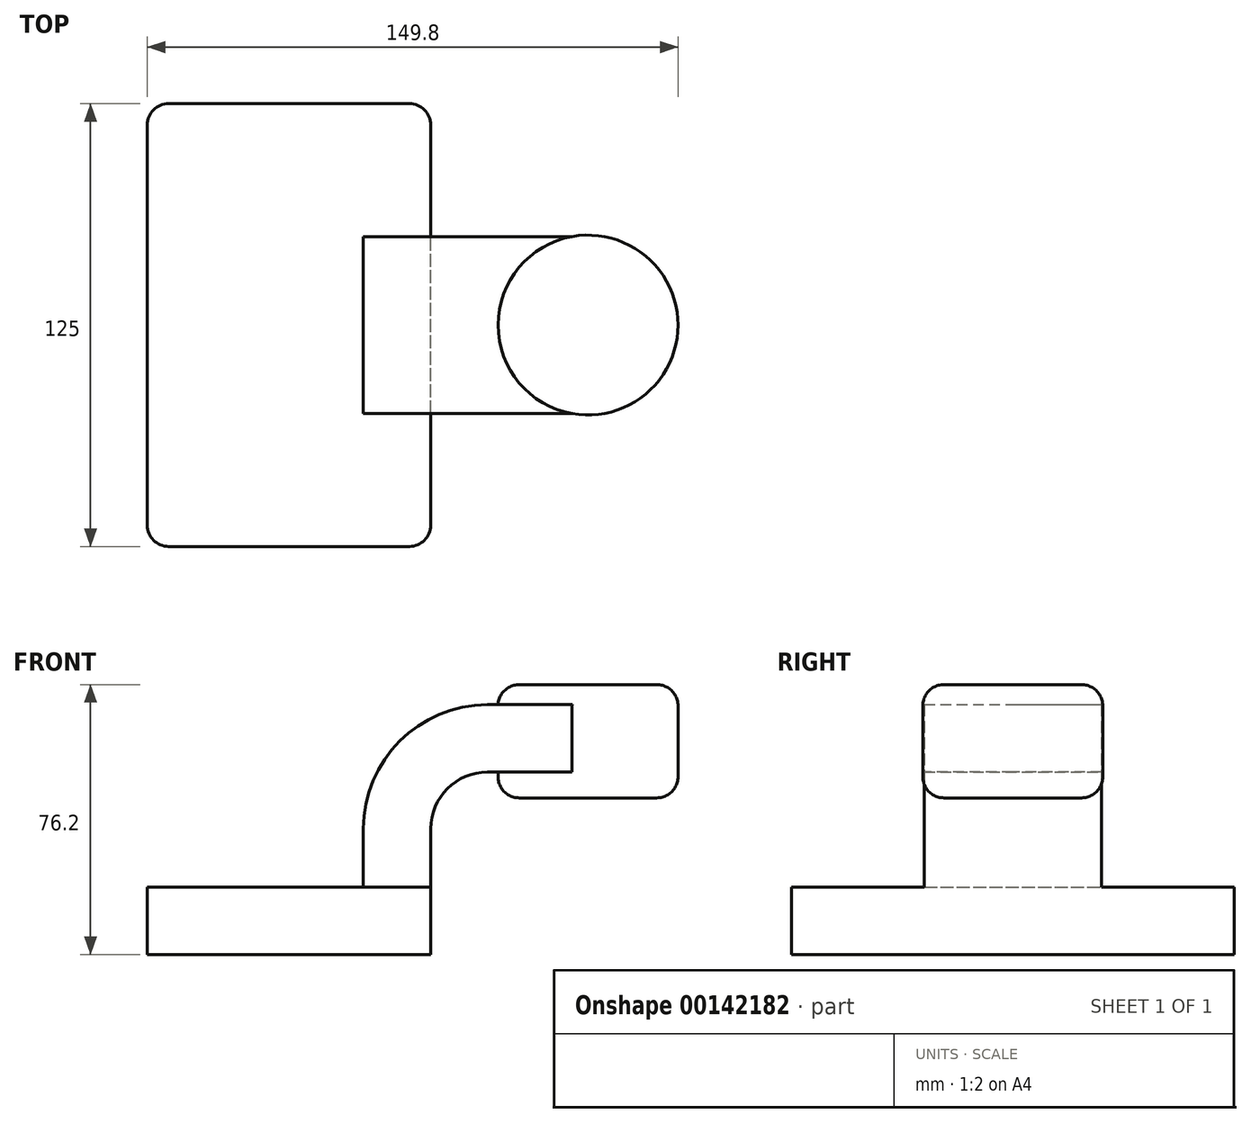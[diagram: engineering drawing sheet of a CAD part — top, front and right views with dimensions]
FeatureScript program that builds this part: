
annotation { "Feature Type Name" : "Feature", "Feature Type Description" : "" }
export const myFeature = defineFeature(function(context is Context, id is Id, definition is map)
    precondition{}
    {
        {
            var Q0;
            Q0=qCreatedBy(makeId("Front.planeOp"),FACE);
            var sketch = newSketch(context, id + "F0", { "sketchPlane" : qUnion([Q0])});
            skLineSegment(sketch, "E0.bottom", {"start": v(-40, -9.5) * mm, "end": v(40, -9.5) * mm});
            skLineSegment(sketch, "E0.top", {"start": v(-40, 9.5) * mm, "end": v(40, 9.5) * mm});
            skLineSegment(sketch, "E0.left", {"start": v(-40, -9.5) * mm, "end": v(-40, 9.5) * mm});
            skLineSegment(sketch, "E0.right", {"start": v(40, -9.5) * mm, "end": v(40, 9.5) * mm});
            skPoint(sketch, "E0.middle", {"position": v(0, 0) * mm});
            skLineSegment(sketch, "E1", {"start": v(40, 9.5) * mm, "end": v(40, 26) * mm});
            skArc(sketch, "E2", {"start": v(40, 26) * mm, "mid": v(44.69, 37.31) * mm, "end": v(56, 42) * mm});
            skLineSegment(sketch, "E3.bottom", {"start": v(59, 34.7) * mm, "end": v(109.8, 34.7) * mm});
            skLineSegment(sketch, "E3.top", {"start": v(59, 66.7) * mm, "end": v(109.8, 66.7) * mm});
            skLineSegment(sketch, "E3.left", {"start": v(59, 34.7) * mm, "end": v(59, 66.7) * mm});
            skLineSegment(sketch, "E3.right", {"start": v(109.8, 34.7) * mm, "end": v(109.8, 66.7) * mm});
            skPoint(sketch, "E3.middle", {"position": v(84.4, 50.7) * mm});
            skLineSegment(sketch, "E4", {"start": v(56, 42) * mm, "end": v(84.4, 42) * mm});
            skLineSegment(sketch, "E5.0", {"start": v(56, 61) * mm, "end": v(84.4, 61) * mm});
            skArc(sketch, "E5.1", {"start": v(21, 26) * mm, "mid": v(31.25, 50.75) * mm, "end": v(56, 61) * mm});
            skLineSegment(sketch, "E5.2", {"start": v(21, 9.5) * mm, "end": v(21, 26) * mm});
            skFitSpline(sketch, "E6", {"points": [v(-40, 9.5) * mm, v(56, 61) * mm], "startDerivative": vector(11.83, 64.45) * mm, "endDerivative": vector(168, -2.6) * mm});
            skLineSegment(sketch, "E7", {"start": v(84.4, 34.7) * mm, "end": v(84.4, 66.7) * mm});
            skSolve(sketch);
        }
        {
            var Q0;
            Q0=makeQuery(id+"F0.imprint","IMPRINT",FACE,{"disambiguationData":[TD([[makeQuery(id+"F0.imprint","IMPRINT",EDGE,{"derivedFrom":sQuery(id+"F0.wireOp",EDGE,"E0.bottom")}),1.0]])]});
            extrude(context, id + "F1", {"entities" : qUnion([Q0]), "endBound" : BoundingType.SYMMETRIC, "depth" : 125 * mm});
        }
        {
            var Q0;
            {var subQ5=sQuery(id+"F0.wireOp",EDGE,"E1");Q0=makeQuery(id+"F0.imprint","IMPRINT",FACE,{"disambiguationData":[TD([[makeQuery(id+"F0.imprint","IMPRINT",EDGE,{"derivedFrom":subQ5}),1.0]])]});}
            var Q1;
            {var subQ0=sQuery(id+"F0.wireOp",EDGE,"E4");var subQ1=sQuery(id+"F0.wireOp",EDGE,"E3.left");var subQ2=makeQuery(id+"F0.imprint","INTERSECT",VERTEX,{"derivedFrom":[subQ1,subQ0]});Q1=makeQuery(id+"F0.imprint","IMPRINT",FACE,{"disambiguationData":[TD([[makeQuery(id+"F0.imprint","IMPRINT",EDGE,{"disambiguationData":[TD([[subQ2,-1.0]])],"derivedFrom":subQ1}),-1.0]])]});}
            extrude(context, id + "F2", {"entities" : qUnion([Q0, Q1]), "operationType" : NewBodyOperationType.ADD, "endBound" : BoundingType.SYMMETRIC, "depth" : 50 * mm});
        }
        {
            var Q0;
            Q0=makeQuery(id+"F0.imprint","IMPRINT",FACE,{"disambiguationData":[TD([[makeQuery(id+"F0.imprint","IMPRINT",EDGE,{"derivedFrom":sQuery(id+"F0.wireOp",EDGE,"E5.1")}),1.0]])]});
            extrude(context, id + "F3", {"entities" : qUnion([Q0]), "operationType" : NewBodyOperationType.ADD, "depth" : 16 * mm});
        }
        {
            var Q0;
            {var subQ5=sQuery(id+"F0.wireOp",EDGE,"E3.right");Q0=makeQuery(id+"F0.imprint","IMPRINT",FACE,{"disambiguationData":[TD([[makeQuery(id+"F0.imprint","IMPRINT",EDGE,{"derivedFrom":subQ5}),1.0]])]});}
            var Q1;
            Q1=sQuery(id+"F0.wireOp",EDGE,"E7");
            revolve(context, id + "F4", {"operationType" : NewBodyOperationType.ADD, "entities" : qUnion([Q0]), "axis" : qUnion([Q1]), "revolveType" : RevolveType.FULL});
        }
        {
            var Q0;
            Q0=makeQuery(id+"F1.opExtrude","CAP_EDGE",EDGE,{"disambiguationData":[OSD([sQuery(id+"F0.wireOp",EDGE,"E0.left")])],"isStart":false});
            var Q1;
            Q1=makeQuery(id+"F1.opExtrude","CAP_EDGE",EDGE,{"disambiguationData":[OSD([sQuery(id+"F0.wireOp",EDGE,"E0.right")])],"isStart":false});
            var Q2;
            Q2=makeQuery(id+"F1.opExtrude","CAP_EDGE",EDGE,{"disambiguationData":[OSD([sQuery(id+"F0.wireOp",EDGE,"E0.right")])],"isStart":true});
            var Q3;
            Q3=makeQuery(id+"F1.opExtrude","CAP_EDGE",EDGE,{"disambiguationData":[OSD([sQuery(id+"F0.wireOp",EDGE,"E0.left")])],"isStart":true});
            var Q4;
            Q4=makeQuery(id+"F4.opRevolve","SWEPT_EDGE",EDGE,{"disambiguationData":[OSD([sQuery(id+"F0.wireOp",EDGE,"E3.bottom"),sQuery(id+"F0.wireOp",EDGE,"E3.right")])]});
            var Q5;
            Q5=makeQuery(id+"F4.opRevolve","SWEPT_EDGE",EDGE,{"disambiguationData":[OSD([sQuery(id+"F0.wireOp",EDGE,"E3.top"),sQuery(id+"F0.wireOp",EDGE,"E3.right")])]});
            fillet(context, id + "F5", {"entities" : qUnion([Q0, Q1, Q2, Q3, Q4, Q5]), "radius" : 6 * mm, "tangentPropagation" : true, "allowEdgeOverflow" : false});
        }
    });
